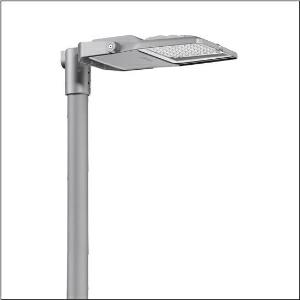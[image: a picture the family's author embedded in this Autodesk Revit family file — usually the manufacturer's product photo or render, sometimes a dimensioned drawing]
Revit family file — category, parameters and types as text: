
# Revit family: floodlight_fl_21_iq_mini___pl64_5xa7772d4e3a_9d14
name_source: partatom
category: Lighting Fixtures
units: mm (PartAtom-declared; Revit-internal decimal feet)

## family parameters
Cut with Voids When Loaded = No
Host = Face
Light Source = No
Part Type = Normal
Room Calculation Point = No
Round Connector Dimension = Use Diameter
Shared = No

## types (1)
- --- (1 x LED, 17970 lm, 143 W, 4000K)
    Apparent Load = 143 VA
    CIE Flux Codes = 28 80 98 100 100
    Color Rendering = 70
    Color Temperature = 4000K
    Default Elevation = 1800 mm
    Description = Floodlight FL 21 iQ mini, floodlight, primary light control with lens, of PMMA, primary optical cover: protective disc, of toughened safety glass, transparent, light distribution: PL64, light emission: direct distribution, installation type: surface-mounted, lamps: LED, High Power LED, rated values: 17.970lm | 143W | 125,7lm/W (begin service life); end service life: 17.970lm | 151,6W; at 50% lumin. flux: 8.985lm | 60,8W | 147,8lm/W, colour temperature: 4000K, colour rendering: CRI > 70, light colour: 740, light setting 1 begin service life: 100% | 17.970lm | 143W | 125,7lm/W | 4.000K, light setting 1 end service life: 151,6W, further light settings possible, control: pre-setting: linear dimming characteristic, Auto-Match, Temp-Guard, Night-Set, Smart-Wire, Desk-Remote (wireless, voltage-free reading and setting of iQ features in the workshop via application-optimized NFC function/RFID function), optimised constant luminous flux control (CLO 2.0), Light-Fading, Lumen-Switch, with terminal, 6-pole, mains connection: 220..240V, AC, 50/60Hz, luminaire housing, of diecast aluminium, powder-coated, SITECO metallic grey (DB 702S), corrosivity category C5 mid according to DIN EN ISO 12944suitable for swimming poolschlorine-resistant, sealing non-destructively replaceable, please order mast flange separately, mast bracket, of steel, galvanised, powder-coated, protection rating (complete): IP66, insulation class (complete): insulation class II (safety insulation), certification: CE, ENEC, VDE, protection symbol: D, impact resistance: IK08, permissible operating ambient temperature: -40..+40°C, permissible operating ambient temperature for outdoor applications: -40..+50°C, standard: DIN EN 12944, LABS conformity tested according to VDMA 24364:2018-05, packaging unit: 1 piece

Light Distribution: PL64
    Height = 70 mm
    Lamp = 1 x LED
    Lamp Light Flux = 17970 lm
    Lamp Power = 143 W
    Lamp count = 1
    Length = 485 mm
    Luminous efficacy = 126 lm/W
    Manufacturer = Siteco
    ModVariant = No
    Model = 5XA7772D4E3A
    Mounting Place = Pole
    Mounting Type = Pole annexe
    Number of Poles = 1
    OnlyDefault = Yes
    Power Factor = 1
    Product Name = Floodlight FL 21 iQ mini | PL64
    Product group = floodlight | pylon annexe
    ProductGroupID = 6201
    Protection Class = Protection class II
    Protection Degree = IP 66
    RLX_Detail_Level = 1
    RLX_Emergency_Light_Flux = 0 lm
    RLX_Emergency_Type = 0
    RLX_Emergency_Type_DB = No
    RlxData = <blob elided: 101797 chars, md5=c0f64596>
    Socket = socket
    Standby Power = 0 W
    System Light Flux = 17970 lm
    System Power = 143 W
    Type Comments = factory setting: luminous flux: 100 % | dim-lin: 254 | 730 mA
    Type Image = l_1007125.jpg
    URL = http://relux.com
    VarID = @adj_166683
    Voltage = 0 V
    Weight = 0.00 kg
    Width = 337 mm

## geometry (parser evidence)
native form markers: Blend x4, Sweep x12
no freeform markers — native parametric forms only
